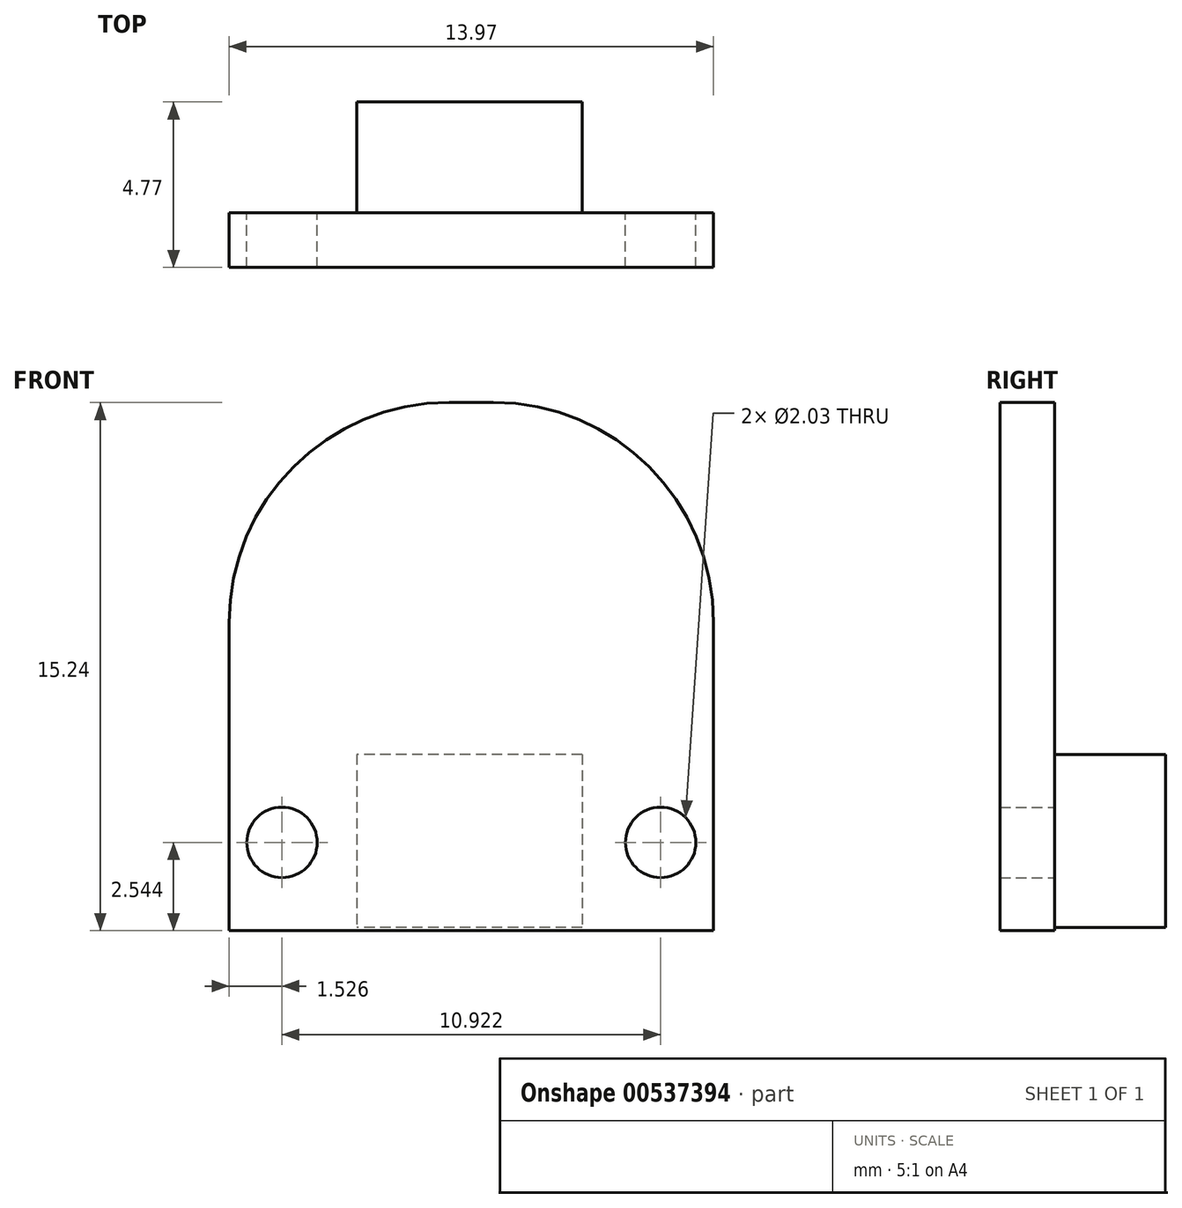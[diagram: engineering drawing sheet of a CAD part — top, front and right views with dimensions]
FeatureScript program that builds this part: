
annotation { "Feature Type Name" : "Feature", "Feature Type Description" : "" }
export const myFeature = defineFeature(function(context is Context, id is Id, definition is map)
    precondition{}
    {
        {
            var Q0;
            Q0=qCreatedBy(makeId("Front.planeOp"),FACE);
            var sketch = newSketch(context, id + "F0", { "sketchPlane" : qUnion([Q0])});
            skLineSegment(sketch, "E0.bottom", {"start": v(-0.58, 8.9) * mm, "end": v(0.7, 8.9) * mm});
            skLineSegment(sketch, "E0.top", {"start": v(-6.93, -6.34) * mm, "end": v(7.04, -6.34) * mm});
            skLineSegment(sketch, "E0.left", {"start": v(-6.93, 2.55) * mm, "end": v(-6.93, -6.34) * mm});
            skLineSegment(sketch, "E0.right", {"start": v(7.04, 2.55) * mm, "end": v(7.04, -6.34) * mm});
            skPoint(sketch, "E1.visualSharp", {"position": v(-6.93, 8.9) * mm});
            skArc(sketch, "E1.filletArc", {"start": v(-0.58, 8.9) * mm, "mid": v(-5.07, 7.04) * mm, "end": v(-6.93, 2.55) * mm});
            skPoint(sketch, "E2.visualSharp", {"position": v(7.04, 8.9) * mm});
            skArc(sketch, "E2.filletArc", {"start": v(7.04, 2.55) * mm, "mid": v(5.18, 7.04) * mm, "end": v(0.7, 8.9) * mm});
            skCircle(sketch, "E3", {"center": v(-5.4, -3.8) * mm, "radius": 1.02 * mm});
            skCircle(sketch, "E4", {"center": v(5.52, -3.8) * mm, "radius": 1.02 * mm});
            skLineSegment(sketch, "E5", {"start": v(-5.4, -3.8) * mm, "end": v(-6.93, -3.8) * mm, "construction": true});
            skLineSegment(sketch, "E6", {"start": v(-5.4, -3.8) * mm, "end": v(-5.4, -6.34) * mm, "construction": true});
            skLineSegment(sketch, "E7", {"start": v(5.52, -3.8) * mm, "end": v(5.52, -6.34) * mm, "construction": true});
            skLineSegment(sketch, "E8", {"start": v(5.52, -3.8) * mm, "end": v(7.04, -3.8) * mm, "construction": true});
            skLineSegment(sketch, "E9", {"start": v(7.04, -1.26) * mm, "end": v(-6.93, -1.26) * mm, "construction": true});
            skLineSegment(sketch, "E10", {"start": v(0.06, 8.9) * mm, "end": v(0, -1.26) * mm, "construction": true});
            skSolve(sketch);
        }
        {
            var Q0;
            Q0=makeQuery(id+"F0.imprint","IMPRINT",FACE,{"disambiguationData":[TD([[makeQuery(id+"F0.imprint","IMPRINT",EDGE,{"derivedFrom":sQuery(id+"F0.wireOp",EDGE,"E0.bottom")}),-1.0]])]});
            extrude(context, id + "F1", {"entities" : qUnion([Q0]), "depth" : 1.57 * mm, "offsetDistance" : 25.4 * mm});
        }
        {
            var Q0;
            Q0=makeQuery(id+"F0.imprint","IMPRINT",FACE,{"disambiguationData":[TD([[makeQuery(id+"F0.imprint","IMPRINT",EDGE,{"derivedFrom":sQuery(id+"F0.wireOp",EDGE,"E0.bottom")}),-1.0]])]});
            var sketch = newSketch(context, id + "F2", { "sketchPlane" : qUnion([Q0])});
            skLineSegment(sketch, "E11.bottom", {"start": v(3.25, -1.26) * mm, "end": v(-3.25, -1.26) * mm});
            skLineSegment(sketch, "E11.top", {"start": v(3.25, -6.26) * mm, "end": v(-3.25, -6.26) * mm});
            skLineSegment(sketch, "E11.left", {"start": v(3.25, -1.26) * mm, "end": v(3.25, -6.26) * mm});
            skLineSegment(sketch, "E11.right", {"start": v(-3.25, -1.26) * mm, "end": v(-3.25, -6.26) * mm});
            skSolve(sketch);
        }
        {
            var Q0;
            Q0=makeQuery(id+"F2.imprint","IMPRINT",FACE,{"disambiguationData":[TD([[makeQuery(id+"F2.imprint","IMPRINT",EDGE,{"derivedFrom":sQuery(id+"F2.wireOp",EDGE,"E11.bottom")}),1.0]])]});
            extrude(context, id + "F3", {"entities" : qUnion([Q0]), "operationType" : NewBodyOperationType.ADD, "oppositeDirection" : true, "depth" : 3.2 * mm, "offsetDistance" : 25.4 * mm});
        }
    });
